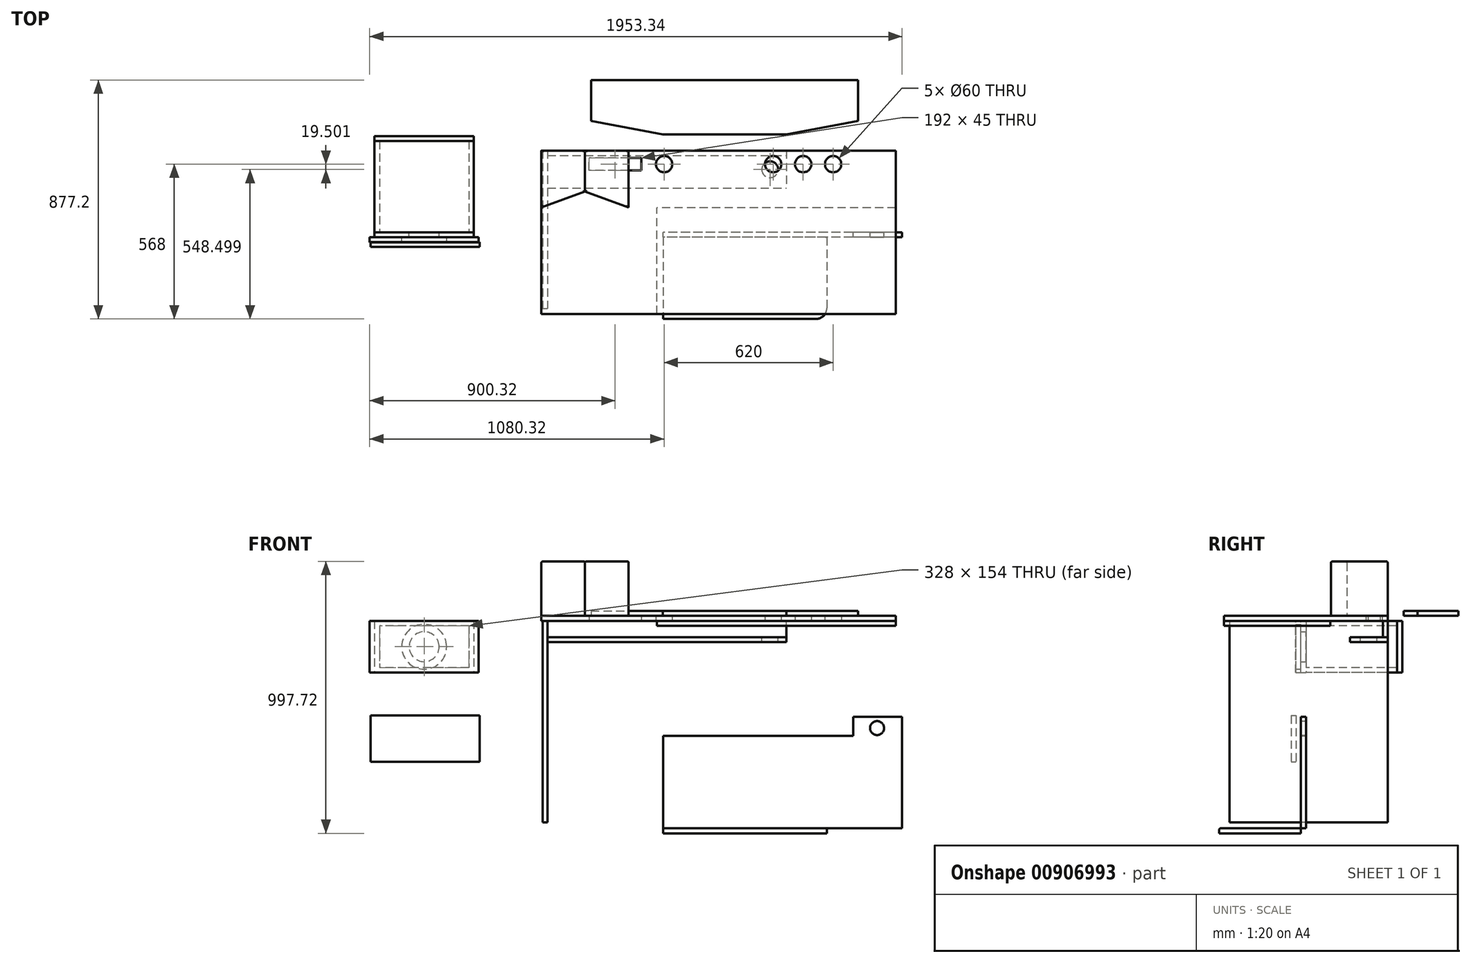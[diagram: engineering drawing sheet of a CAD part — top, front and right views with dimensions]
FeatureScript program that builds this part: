
annotation { "Feature Type Name" : "Feature", "Feature Type Description" : "" }
export const myFeature = defineFeature(function(context is Context, id is Id, definition is map)
    precondition{}
    {
        {
            var Q0;
            Q0=qCreatedBy(makeId("Top.planeOp"),FACE);
            var sketch = newSketch(context, id + "F0", { "sketchPlane" : qUnion([Q0])});
            skLineSegment(sketch, "E0.bottom", {"start": v(650, -300) * mm, "end": v(-650, -300) * mm});
            skLineSegment(sketch, "E0.top", {"start": v(650, 300) * mm, "end": v(-650, 300) * mm});
            skLineSegment(sketch, "E0.left", {"start": v(650, -300) * mm, "end": v(650, 300) * mm});
            skLineSegment(sketch, "E0.right", {"start": v(-650, -300) * mm, "end": v(-650, 300) * mm});
            skPoint(sketch, "E0.middle", {"position": v(0, 0) * mm});
            skLineSegment(sketch, "E1", {"start": v(-650, 250) * mm, "end": v(650, 250) * mm, "construction": true});
            skCircle(sketch, "E2", {"center": v(420, 250) * mm, "radius": 30 * mm});
            skCircle(sketch, "E3.1.0.0", {"center": v(-200, 250) * mm, "radius": 30 * mm});
            skCircle(sketch, "E3.2.0.0", {"center": v(200, 250) * mm, "radius": 30 * mm});
            skCircle(sketch, "E3.3.0.0", {"center": v(310, 250) * mm, "radius": 30 * mm});
            skLineSegment(sketch, "E3.direction1", {"start": v(-200, 250) * mm, "end": v(420, 250) * mm, "construction": true});
            skLineSegment(sketch, "E4.bottom", {"start": v(-284, 227.5) * mm, "end": v(-476, 227.5) * mm});
            skLineSegment(sketch, "E4.top", {"start": v(-284, 272.5) * mm, "end": v(-476, 272.5) * mm});
            skLineSegment(sketch, "E4.left", {"start": v(-284, 227.5) * mm, "end": v(-284, 272.5) * mm});
            skLineSegment(sketch, "E4.right", {"start": v(-476, 227.5) * mm, "end": v(-476, 272.5) * mm});
            skPoint(sketch, "E4.middle", {"position": v(-380, 250) * mm});
            skSolve(sketch);
        }
        {
            var Q0;
            Q0=qSketchRegion(id+"F0",true);
            extrude(context, id + "F1", {"entities" : qUnion([Q0]), "depth" : 18 * mm, "offsetDistance" : 25 * mm});
        }
        {
            var Q0;
            Q0=makeQuery(id+"F1.opExtrude","CAP_FACE",FACE,{"disambiguationData":[OSD([sQuery(id+"F0.wireOp",EDGE,"E0.bottom"),sQuery(id+"F0.wireOp",EDGE,"E0.top"),sQuery(id+"F0.wireOp",EDGE,"E0.left"),sQuery(id+"F0.wireOp",EDGE,"E0.right")])],"isStart":true});
            var sketch = newSketch(context, id + "F2", { "sketchPlane" : qUnion([Q0])});
            skLineSegment(sketch, "E5.bottom", {"start": v(-627.74, -300) * mm, "end": v(248.26, -300) * mm});
            skLineSegment(sketch, "E5.top", {"start": v(-627.74, -282) * mm, "end": v(248.26, -282) * mm});
            skLineSegment(sketch, "E5.left", {"start": v(-627.74, -300) * mm, "end": v(-627.74, -282) * mm});
            skLineSegment(sketch, "E5.right", {"start": v(248.26, -300) * mm, "end": v(248.26, -282) * mm});
            skSolve(sketch);
        }
        {
            var Q0;
            Q0=qSketchRegion(id+"F2",true);
            extrude(context, id + "F3", {"entities" : qUnion([Q0]), "depth" : 60 * mm, "offsetDistance" : 25 * mm});
        }
        {
            var Q0;
            Q0=makeQuery(id+"F3.opExtrude","CAP_FACE",FACE,{"disambiguationData":[OSD([sQuery(id+"F2.wireOp",EDGE,"E5.bottom"),sQuery(id+"F2.wireOp",EDGE,"E5.top"),sQuery(id+"F2.wireOp",EDGE,"E5.left"),sQuery(id+"F2.wireOp",EDGE,"E5.right")])],"isStart":false});
            var sketch = newSketch(context, id + "F4", { "sketchPlane" : qUnion([Q0])});
            skLineSegment(sketch, "E6.bottom", {"start": v(-627.74, -300) * mm, "end": v(248.26, -300) * mm});
            skLineSegment(sketch, "E6.top", {"start": v(-627.74, -162) * mm, "end": v(248.26, -162) * mm});
            skLineSegment(sketch, "E6.left", {"start": v(-627.74, -300) * mm, "end": v(-627.74, -162) * mm});
            skLineSegment(sketch, "E6.right", {"start": v(248.26, -300) * mm, "end": v(248.26, -162) * mm});
            skCircle(sketch, "E7", {"center": v(188.26, -230.5) * mm, "radius": 30 * mm});
            skSolve(sketch);
        }
        {
            var Q0;
            Q0=qSketchRegion(id+"F4",true);
            extrude(context, id + "F5", {"entities" : qUnion([Q0]), "depth" : 18 * mm, "offsetDistance" : 25 * mm});
        }
        {
            var Q0;
            Q0=makeQuery(id+"F3.opExtrude","SWEPT_FACE",FACE,{"disambiguationData":[OSD([sQuery(id+"F2.wireOp",EDGE,"E5.left")])]});
            var sketch = newSketch(context, id + "F6", { "sketchPlane" : qUnion([Q0])});
            skLineSegment(sketch, "E8.bottom", {"start": v(-300, 0) * mm, "end": v(280, 0) * mm});
            skLineSegment(sketch, "E8.top", {"start": v(-300, -740) * mm, "end": v(280, -740) * mm});
            skLineSegment(sketch, "E8.left", {"start": v(-300, 0) * mm, "end": v(-300, -740) * mm});
            skLineSegment(sketch, "E8.right", {"start": v(280, 0) * mm, "end": v(280, -740) * mm});
            skSolve(sketch);
        }
        {
            var Q0;
            Q0=qSketchRegion(id+"F6",true);
            extrude(context, id + "F7", {"entities" : qUnion([Q0]), "depth" : 18 * mm, "offsetDistance" : 25 * mm});
        }
        {
            var Q0;
            Q0=makeQuery(id+"F1.opExtrude","CAP_FACE",FACE,{"disambiguationData":[OSD([sQuery(id+"F0.wireOp",EDGE,"E0.bottom"),sQuery(id+"F0.wireOp",EDGE,"E0.top"),sQuery(id+"F0.wireOp",EDGE,"E0.left"),sQuery(id+"F0.wireOp",EDGE,"E0.right")])],"isStart":false});
            var sketch = newSketch(context, id + "F8", { "sketchPlane" : qUnion([Q0])});
            skLineSegment(sketch, "E9", {"start": v(-650, 300) * mm, "end": v(-650, 91.76) * mm});
            skLineSegment(sketch, "E10", {"start": v(-650, 91.76) * mm, "end": v(-490, 150) * mm});
            skLineSegment(sketch, "E11", {"start": v(-490, 150) * mm, "end": v(-490, 300) * mm});
            skLineSegment(sketch, "E12", {"start": v(-490, 300) * mm, "end": v(-650, 300) * mm});
            skSolve(sketch);
        }
        {
            var Q0;
            Q0=qSketchRegion(id+"F8",true);
            extrude(context, id + "F9", {"entities" : qUnion([Q0]), "depth" : 200 * mm, "offsetDistance" : 25 * mm});
        }
        {
            var Q0;
            Q0=qCreatedBy(makeId("Front.planeOp"),FACE);
            var sketch = newSketch(context, id + "F10", { "sketchPlane" : qUnion([Q0])});
            skLineSegment(sketch, "E13.bottom", {"start": v(-1262.32, 0) * mm, "end": v(-898.32, 0) * mm});
            skLineSegment(sketch, "E13.top", {"start": v(-1262.32, -190) * mm, "end": v(-898.32, -190) * mm});
            skLineSegment(sketch, "E13.left", {"start": v(-1262.32, 0) * mm, "end": v(-1262.32, -190) * mm});
            skLineSegment(sketch, "E13.right", {"start": v(-898.32, 0) * mm, "end": v(-898.32, -190) * mm});
            skCircle(sketch, "E14", {"center": v(-1080.32, -95) * mm, "radius": 55 * mm});
            skPoint(sketch, "E14.centerSnap0", {"position": v(-1080.32, -190) * mm});
            skPoint(sketch, "E14.centerSnap1", {"position": v(-1262.32, -95) * mm});
            skSolve(sketch);
        }
        {
            var Q0;
            Q0=qSketchRegion(id+"F10",true);
            extrude(context, id + "F11", {"entities" : qUnion([Q0]), "depth" : 18 * mm, "offsetDistance" : 25 * mm});
        }
        {
            var Q0;
            Q0=makeQuery(id+"F11.opExtrude","CAP_FACE",FACE,{"disambiguationData":[OSD([sQuery(id+"F10.wireOp",EDGE,"E13.bottom"),sQuery(id+"F10.wireOp",EDGE,"E13.top"),sQuery(id+"F10.wireOp",EDGE,"E13.left"),sQuery(id+"F10.wireOp",EDGE,"E13.right"),sQuery(id+"F10.wireOp",EDGE,"E14")])],"isStart":true});
            var sketch = newSketch(context, id + "F12", { "sketchPlane" : qUnion([Q0])});
            skLineSegment(sketch, "E15.bottom", {"start": v(898.32, 0) * mm, "end": v(1262.32, 0) * mm});
            skLineSegment(sketch, "E15.top", {"start": v(898.32, -190) * mm, "end": v(1262.32, -190) * mm});
            skLineSegment(sketch, "E15.left", {"start": v(898.32, 0) * mm, "end": v(898.32, -190) * mm});
            skLineSegment(sketch, "E15.right", {"start": v(1262.32, 0) * mm, "end": v(1262.32, -190) * mm});
            skLineSegment(sketch, "E16.bottom", {"start": v(916.32, -18) * mm, "end": v(1244.32, -18) * mm});
            skLineSegment(sketch, "E16.top", {"start": v(916.32, -172) * mm, "end": v(1244.32, -172) * mm});
            skLineSegment(sketch, "E16.left", {"start": v(916.32, -18) * mm, "end": v(916.32, -172) * mm});
            skLineSegment(sketch, "E16.right", {"start": v(1244.32, -18) * mm, "end": v(1244.32, -172) * mm});
            skSolve(sketch);
        }
        {
            var Q0;
            Q0=qSketchRegion(id+"F12",true);
            extrude(context, id + "F13", {"entities" : qUnion([Q0]), "depth" : 335 * mm, "offsetDistance" : 25 * mm});
        }
        {
            var Q0;
            Q0=makeQuery(id+"F11.opExtrude","CAP_FACE",FACE,{"disambiguationData":[OSD([sQuery(id+"F10.wireOp",EDGE,"E13.bottom"),sQuery(id+"F10.wireOp",EDGE,"E13.top"),sQuery(id+"F10.wireOp",EDGE,"E13.left"),sQuery(id+"F10.wireOp",EDGE,"E13.right"),sQuery(id+"F10.wireOp",EDGE,"E14")])],"isStart":false});
            var sketch = newSketch(context, id + "F14", { "sketchPlane" : qUnion([Q0])});
            skLineSegment(sketch, "E17.bottom", {"start": v(-880.32, -190) * mm, "end": v(-1280.32, -190) * mm});
            skLineSegment(sketch, "E17.top", {"start": v(-880.32, 0) * mm, "end": v(-1280.32, 0) * mm});
            skLineSegment(sketch, "E17.left", {"start": v(-880.32, -190) * mm, "end": v(-880.32, 0) * mm});
            skLineSegment(sketch, "E17.right", {"start": v(-1280.32, -190) * mm, "end": v(-1280.32, 0) * mm});
            skPoint(sketch, "E17.middle", {"position": v(-1080.32, -95) * mm});
            skCircle(sketch, "E18", {"center": v(-1080.32, -95) * mm, "radius": 82.5 * mm});
            skSolve(sketch);
        }
        {
            var Q0;
            Q0=qSketchRegion(id+"F14",true);
            extrude(context, id + "F15", {"entities" : qUnion([Q0]), "depth" : 18 * mm, "offsetDistance" : 25 * mm});
        }
        {
            var Q0;
            Q0=makeQuery(id+"F13.opExtrude","CAP_FACE",FACE,{"disambiguationData":[OSD([sQuery(id+"F12.wireOp",EDGE,"E15.bottom"),sQuery(id+"F12.wireOp",EDGE,"E15.top"),sQuery(id+"F12.wireOp",EDGE,"E15.left"),sQuery(id+"F12.wireOp",EDGE,"E15.right"),sQuery(id+"F12.wireOp",EDGE,"E16.bottom"),sQuery(id+"F12.wireOp",EDGE,"E16.top"),sQuery(id+"F12.wireOp",EDGE,"E16.left"),sQuery(id+"F12.wireOp",EDGE,"E16.right")])],"isStart":false});
            var sketch = newSketch(context, id + "F16", { "sketchPlane" : qUnion([Q0])});
            skLineSegment(sketch, "E19.bottom", {"start": v(898.32, 0) * mm, "end": v(1262.32, 0) * mm});
            skLineSegment(sketch, "E19.top", {"start": v(898.32, -190) * mm, "end": v(1262.32, -190) * mm});
            skLineSegment(sketch, "E19.left", {"start": v(898.32, 0) * mm, "end": v(898.32, -190) * mm});
            skLineSegment(sketch, "E19.right", {"start": v(1262.32, 0) * mm, "end": v(1262.32, -190) * mm});
            skSolve(sketch);
        }
        {
            var Q0;
            Q0=qSketchRegion(id+"F16",true);
            extrude(context, id + "F17", {"entities" : qUnion([Q0]), "depth" : 18 * mm, "offsetDistance" : 25 * mm});
        }
        {
            var Q0;
            Q0=makeQuery(id+"F1.opExtrude","CAP_FACE",FACE,{"disambiguationData":[OSD([sQuery(id+"F0.wireOp",EDGE,"E0.bottom"),sQuery(id+"F0.wireOp",EDGE,"E0.top"),sQuery(id+"F0.wireOp",EDGE,"E0.left"),sQuery(id+"F0.wireOp",EDGE,"E0.right"),sQuery(id+"F0.wireOp",EDGE,"E2"),sQuery(id+"F0.wireOp",EDGE,"E3.1.0.0"),sQuery(id+"F0.wireOp",EDGE,"E3.2.0.0"),sQuery(id+"F0.wireOp",EDGE,"E3.3.0.0"),sQuery(id+"F0.wireOp",EDGE,"E4.bottom"),sQuery(id+"F0.wireOp",EDGE,"E4.top"),sQuery(id+"F0.wireOp",EDGE,"E4.left"),sQuery(id+"F0.wireOp",EDGE,"E4.right")])],"isStart":true});
            var sketch = newSketch(context, id + "F18", { "sketchPlane" : qUnion([Q0])});
            skLineSegment(sketch, "E20.bottom", {"start": v(650, 300) * mm, "end": v(-226, 300) * mm});
            skLineSegment(sketch, "E20.top", {"start": v(650, -90) * mm, "end": v(-226, -90) * mm});
            skLineSegment(sketch, "E20.left", {"start": v(650, 300) * mm, "end": v(650, -90) * mm});
            skLineSegment(sketch, "E20.right", {"start": v(-226, 300) * mm, "end": v(-226, -90) * mm});
            skSolve(sketch);
        }
        {
            var Q0;
            Q0=qSketchRegion(id+"F18",true);
            extrude(context, id + "F19", {"entities" : qUnion([Q0]), "depth" : 18 * mm, "offsetDistance" : 25 * mm});
        }
        {
            var Q0;
            Q0=qCreatedBy(makeId("Front.planeOp"),FACE);
            var sketch = newSketch(context, id + "F20", { "sketchPlane" : qUnion([Q0])});
            skLineSegment(sketch, "E21.top", {"start": v(673.02, -761.72) * mm, "end": v(-202.98, -761.72) * mm});
            skLineSegment(sketch, "E21.left", {"start": v(673.02, -351.72) * mm, "end": v(673.02, -761.72) * mm});
            skLineSegment(sketch, "E22", {"start": v(673.02, -351.72) * mm, "end": v(493.02, -351.72) * mm});
            skLineSegment(sketch, "E23", {"start": v(493.02, -351.72) * mm, "end": v(493.02, -421.72) * mm});
            skLineSegment(sketch, "E24", {"start": v(493.02, -421.72) * mm, "end": v(-202.98, -421.72) * mm});
            skLineSegment(sketch, "E25", {"start": v(-202.98, -421.72) * mm, "end": v(-202.98, -761.72) * mm});
            skCircle(sketch, "E26", {"center": v(581.1, -393.66) * mm, "radius": 25.73 * mm});
            skSolve(sketch);
        }
        {
            var Q0;
            Q0=qSketchRegion(id+"F20",true);
            extrude(context, id + "F21", {"entities" : qUnion([Q0]), "depth" : 18 * mm, "offsetDistance" : 25 * mm});
        }
        {
            var Q0;
            Q0=makeQuery(id+"F21.opExtrude","SWEPT_FACE",FACE,{"disambiguationData":[OSD([sQuery(id+"F20.wireOp",EDGE,"E21.top")])]});
            var sketch = newSketch(context, id + "F22", { "sketchPlane" : qUnion([Q0])});
            skLineSegment(sketch, "E27.bottom", {"start": v(-202.98, 18) * mm, "end": v(397.02, 18) * mm});
            skLineSegment(sketch, "E27.top", {"start": v(-202.98, 318) * mm, "end": v(357.02, 318) * mm});
            skLineSegment(sketch, "E27.left", {"start": v(-202.98, 18) * mm, "end": v(-202.98, 318) * mm});
            skLineSegment(sketch, "E27.right", {"start": v(397.02, 18) * mm, "end": v(397.02, 278) * mm});
            skPoint(sketch, "E28.visualSharp", {"position": v(397.02, 318) * mm});
            skArc(sketch, "E28.filletArc", {"start": v(397.02, 278) * mm, "mid": v(385.3, 306.28) * mm, "end": v(357.02, 318) * mm});
            skSolve(sketch);
        }
        {
            var Q0;
            Q0=qSketchRegion(id+"F22",true);
            extrude(context, id + "F23", {"entities" : qUnion([Q0]), "depth" : 18 * mm, "offsetDistance" : 25 * mm});
        }
        {
            var Q0;
            Q0=makeQuery(id+"F23.opExtrude","CAP_EDGE",EDGE,{"disambiguationData":[OSD([sQuery(id+"F22.wireOp",EDGE,"E27.top")])],"isStart":true});
            var Q1;
            Q1=makeQuery(id+"F23.opExtrude","CAP_EDGE",EDGE,{"disambiguationData":[OSD([sQuery(id+"F22.wireOp",EDGE,"E28.filletArc")])],"isStart":true});
            var Q2;
            Q2=makeQuery(id+"F23.opExtrude","CAP_EDGE",EDGE,{"disambiguationData":[OSD([sQuery(id+"F22.wireOp",EDGE,"E27.right")])],"isStart":true});
            fillet(context, id + "F24", {"entities" : qUnion([Q0, Q1, Q2]), "radius" : 5 * mm, "tangentPropagation" : true, "allowEdgeOverflow" : false});
        }
        {
            var Q0;
            Q0=makeQuery(id+"F15.opExtrude","CAP_FACE",FACE,{"disambiguationData":[OSD([sQuery(id+"F14.wireOp",EDGE,"E17.bottom"),sQuery(id+"F14.wireOp",EDGE,"E17.top"),sQuery(id+"F14.wireOp",EDGE,"E17.left"),sQuery(id+"F14.wireOp",EDGE,"E17.right"),sQuery(id+"F14.wireOp",EDGE,"E18")])],"isStart":false});
            var sketch = newSketch(context, id + "F25", { "sketchPlane" : qUnion([Q0])});
            skLineSegment(sketch, "E29.bottom", {"start": v(-1276.2, -347.69) * mm, "end": v(-876.2, -347.69) * mm});
            skLineSegment(sketch, "E29.top", {"start": v(-1276.2, -517.69) * mm, "end": v(-876.2, -517.69) * mm});
            skLineSegment(sketch, "E29.left", {"start": v(-1276.2, -347.69) * mm, "end": v(-1276.2, -517.69) * mm});
            skLineSegment(sketch, "E29.right", {"start": v(-876.2, -347.69) * mm, "end": v(-876.2, -517.69) * mm});
            skSolve(sketch);
        }
        {
            var Q0;
            Q0=qSketchRegion(id+"F25",true);
            extrude(context, id + "F26", {"entities" : qUnion([Q0]), "depth" : 18 * mm, "offsetDistance" : 25 * mm});
        }
        {
            var Q0;
            Q0=makeQuery(id+"F15.opExtrude","CAP_FACE",FACE,{"disambiguationData":[OSD([sQuery(id+"F14.wireOp",EDGE,"E17.bottom"),sQuery(id+"F14.wireOp",EDGE,"E17.top"),sQuery(id+"F14.wireOp",EDGE,"E17.left"),sQuery(id+"F14.wireOp",EDGE,"E17.right"),sQuery(id+"F14.wireOp",EDGE,"E18")])],"isStart":false});
            var sketch = newSketch(context, id + "F27", { "sketchPlane" : qUnion([Q0])});
            skLineSegment(sketch, "E30.bottom", {"start": v(-880.32, -190) * mm, "end": v(-1280.32, -190) * mm});
            skLineSegment(sketch, "E30.top", {"start": v(-880.32, 0) * mm, "end": v(-1280.32, 0) * mm});
            skLineSegment(sketch, "E30.left", {"start": v(-880.32, -190) * mm, "end": v(-880.32, 0) * mm});
            skLineSegment(sketch, "E30.right", {"start": v(-1280.32, -190) * mm, "end": v(-1280.32, 0) * mm});
            skSolve(sketch);
        }
        {
            var Q0;
            Q0=qSketchRegion(id+"F27",true);
            extrude(context, id + "F28", {"entities" : qUnion([Q0]), "depth" : 1 * mm, "offsetDistance" : 25 * mm});
        }
        {
            var Q0;
            Q0=makeQuery(id+"F1.opExtrude","CAP_FACE",FACE,{"disambiguationData":[OSD([sQuery(id+"F0.wireOp",EDGE,"E0.bottom"),sQuery(id+"F0.wireOp",EDGE,"E0.top"),sQuery(id+"F0.wireOp",EDGE,"E0.left"),sQuery(id+"F0.wireOp",EDGE,"E0.right"),sQuery(id+"F0.wireOp",EDGE,"E2"),sQuery(id+"F0.wireOp",EDGE,"E3.1.0.0"),sQuery(id+"F0.wireOp",EDGE,"E3.2.0.0"),sQuery(id+"F0.wireOp",EDGE,"E3.3.0.0"),sQuery(id+"F0.wireOp",EDGE,"E4.bottom"),sQuery(id+"F0.wireOp",EDGE,"E4.top"),sQuery(id+"F0.wireOp",EDGE,"E4.left"),sQuery(id+"F0.wireOp",EDGE,"E4.right")])],"isStart":false});
            var sketch = newSketch(context, id + "F29", { "sketchPlane" : qUnion([Q0])});
            skLineSegment(sketch, "E31.top", {"start": v(-468.02, 559.2) * mm, "end": v(511.98, 559.2) * mm});
            skLineSegment(sketch, "E32", {"start": v(-468.02, 559.2) * mm, "end": v(-468.02, 409.2) * mm});
            skLineSegment(sketch, "E33", {"start": v(-468.02, 409.2) * mm, "end": v(-204.45, 359.2) * mm});
            skLineSegment(sketch, "E34", {"start": v(-204.45, 359.2) * mm, "end": v(248.41, 359.2) * mm});
            skLineSegment(sketch, "E35", {"start": v(248.41, 359.2) * mm, "end": v(511.98, 409.2) * mm});
            skLineSegment(sketch, "E36", {"start": v(511.98, 559.2) * mm, "end": v(511.98, 409.2) * mm});
            skSolve(sketch);
        }
        {
            var Q0;
            Q0=qSketchRegion(id+"F29",true);
            extrude(context, id + "F30", {"entities" : qUnion([Q0]), "depth" : 18 * mm, "offsetDistance" : 25 * mm});
        }
        {
            var Q0;
            Q0=makeQuery(id+"F9.opExtrude","CAP_EDGE",EDGE,{"disambiguationData":[OSD([sQuery(id+"F8.wireOp",EDGE,"E9")])],"isStart":false});
            var Q1;
            Q1=makeQuery(id+"F9.opExtrude","CAP_EDGE",EDGE,{"disambiguationData":[OSD([sQuery(id+"F8.wireOp",EDGE,"E10")])],"isStart":false});
            var Q2;
            Q2=makeQuery(id+"F9.opExtrude","CAP_EDGE",EDGE,{"disambiguationData":[OSD([sQuery(id+"F8.wireOp",EDGE,"E11")])],"isStart":false});
            var Q3;
            Q3=makeQuery(id+"F9.opExtrude","CAP_EDGE",EDGE,{"disambiguationData":[OSD([sQuery(id+"F8.wireOp",EDGE,"E12")])],"isStart":false});
            fillet(context, id + "F31", {"entities" : qUnion([Q0, Q1, Q2, Q3]), "radius" : 5 * mm, "tangentPropagation" : true, "allowEdgeOverflow" : false});
        }
        {
            var Q0;
            Q0=makeQuery(id+"F9.opExtrude","SWEPT_BODY",BODY,{"disambiguationData":[OSD([sQuery(id+"F8.wireOp",EDGE,"E9"),sQuery(id+"F8.wireOp",EDGE,"E10"),sQuery(id+"F8.wireOp",EDGE,"E11"),sQuery(id+"F8.wireOp",EDGE,"E12")])]});
            var Q1;
            Q1=makeQuery(id+"F9.opExtrude","SWEPT_FACE",FACE,{"disambiguationData":[OSD([sQuery(id+"F8.wireOp",EDGE,"E11")])]});
            mirror(context, id + "F32", {"entities" : qUnion([Q0]), "mirrorPlane" : qUnion([Q1])});
        }
    });
